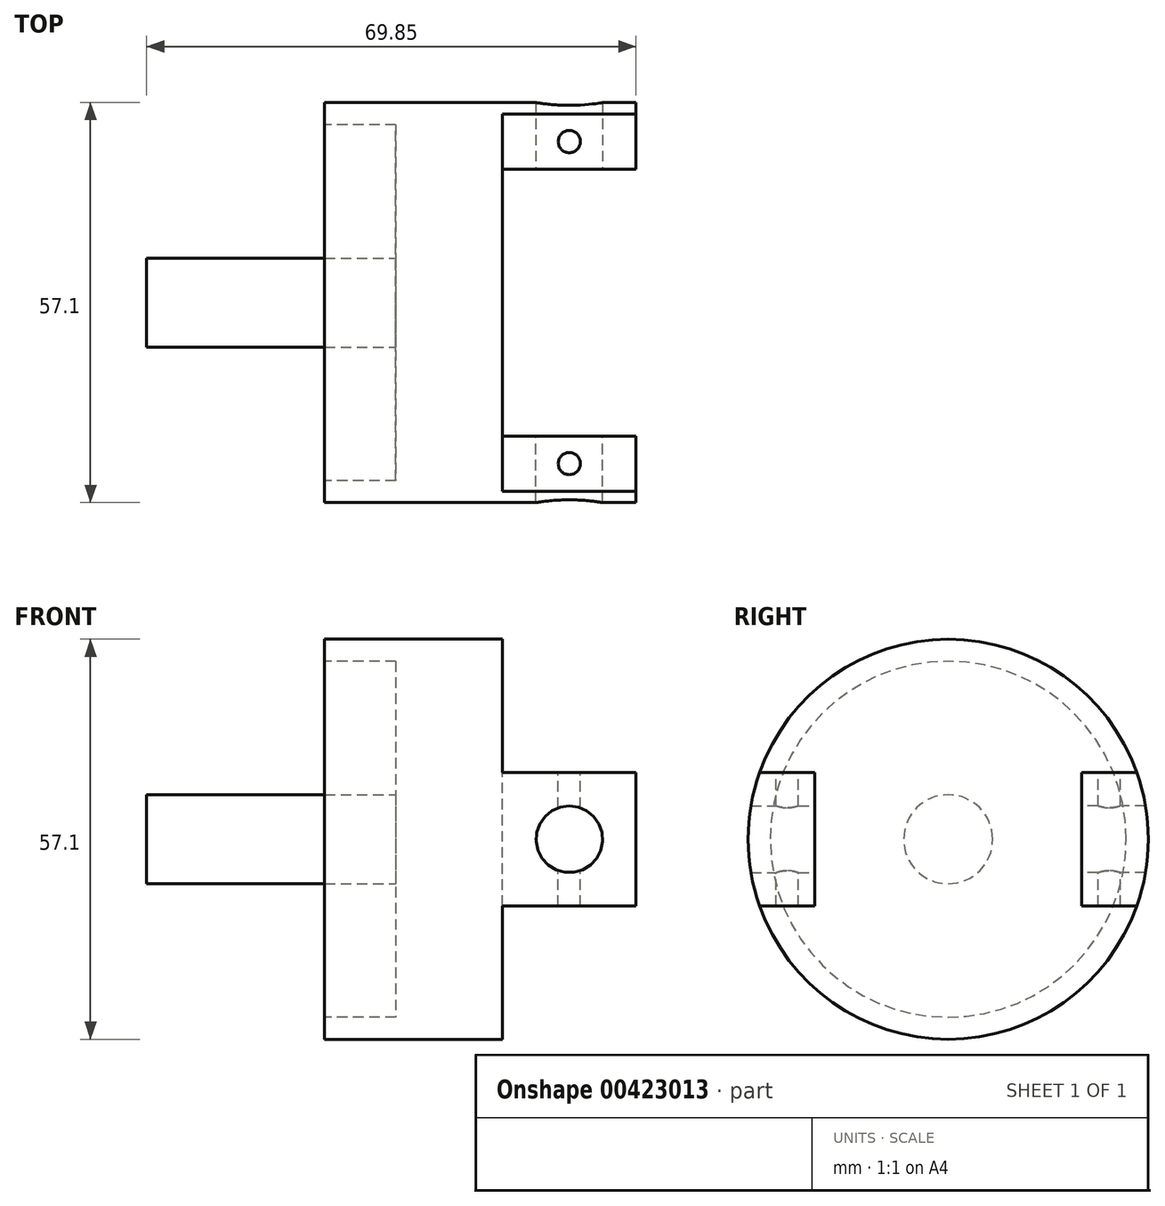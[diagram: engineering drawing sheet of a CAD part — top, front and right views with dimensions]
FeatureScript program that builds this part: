
annotation { "Feature Type Name" : "Feature", "Feature Type Description" : "" }
export const myFeature = defineFeature(function(context is Context, id is Id, definition is map)
    precondition{}
    {
        {
            var Q0;
            Q0=qCreatedBy(makeId("Right.planeOp"),FACE);
            var sketch = newSketch(context, id + "F0", { "sketchPlane" : qUnion([Q0])});
            skCircle(sketch, "E0", {"center": v(0, 0) * mm, "radius": 28.55 * mm});
            skSolve(sketch);
        }
        {
            var Q0;
            Q0 = qSketchRegion(id + "F0", true);
            extrude(context, id + "F1", {"entities" : qUnion([Q0]), "depth" : 38.1 * mm});
        }
        {
            var Q0;
            Q0=qCreatedBy(makeId("Front.planeOp"),FACE);
            var sketch = newSketch(context, id + "F2", { "sketchPlane" : qUnion([Q0])});
            skLineSegment(sketch, "E1.bottom", {"start": v(39.37, 31.7) * mm, "end": v(19.05, 31.7) * mm});
            skLineSegment(sketch, "E1.top", {"start": v(39.37, 9.53) * mm, "end": v(19.05, 9.53) * mm});
            skLineSegment(sketch, "E1.left", {"start": v(39.37, 31.7) * mm, "end": v(39.37, 9.53) * mm});
            skLineSegment(sketch, "E1.right", {"start": v(19.05, 31.7) * mm, "end": v(19.05, 9.53) * mm});
            skLineSegment(sketch, "E2.bottom", {"start": v(39.37, -9.53) * mm, "end": v(19.05, -9.53) * mm});
            skLineSegment(sketch, "E2.top", {"start": v(39.37, -31) * mm, "end": v(19.05, -31) * mm});
            skLineSegment(sketch, "E2.left", {"start": v(39.37, -9.53) * mm, "end": v(39.37, -31) * mm});
            skLineSegment(sketch, "E2.right", {"start": v(19.05, -9.53) * mm, "end": v(19.05, -31) * mm});
            skSolve(sketch);
        }
        {
            var Q0;
            Q0 = qSketchRegion(id + "F2", true);
            extrude(context, id + "F3", {"entities" : qUnion([Q0]), "operationType" : NewBodyOperationType.REMOVE, "oppositeDirection" : true, "depth" : 38.1 * mm, "hasSecondDirection" : true, "secondDirectionOppositeDirection" : false, "secondDirectionDepth" : 38.1 * mm});
        }
        {
            var Q0;
            Q0=qCreatedBy(makeId("Top.planeOp"),FACE);
            var sketch = newSketch(context, id + "F4", { "sketchPlane" : qUnion([Q0])});
            skLineSegment(sketch, "E3.bottom", {"start": v(64.66, 19.05) * mm, "end": v(19.05, 19.05) * mm});
            skLineSegment(sketch, "E3.top", {"start": v(64.66, -19.05) * mm, "end": v(19.05, -19.05) * mm});
            skLineSegment(sketch, "E3.left", {"start": v(64.66, 19.05) * mm, "end": v(64.66, -19.05) * mm});
            skLineSegment(sketch, "E3.right", {"start": v(19.05, 19.05) * mm, "end": v(19.05, -19.05) * mm});
            skPoint(sketch, "E3.middle", {"position": v(41.86, 0) * mm});
            skSolve(sketch);
        }
        {
            var Q0;
            Q0 = qSketchRegion(id + "F4", true);
            extrude(context, id + "F5", {"entities" : qUnion([Q0]), "operationType" : NewBodyOperationType.REMOVE, "oppositeDirection" : true, "depth" : 25.4 * mm, "hasSecondDirection" : true, "secondDirectionOppositeDirection" : false, "secondDirectionDepth" : 25.4 * mm});
        }
        {
            var Q0;
            Q0=makeQuery(id+"F5.boolean.opBoolean","COPY",FACE,{"derivedFrom":makeQuery(id+"F5.opExtrude","SWEPT_FACE",FACE,{"disambiguationData":[OSD([sQuery(id+"F4.wireOp",EDGE,"E3.bottom")])]})});
            var sketch = newSketch(context, id + "F6", { "sketchPlane" : qUnion([Q0])});
            skPoint(sketch, "E4", {"position": v(28.58, 0) * mm});
            skPoint(sketch, "E4.positionSnap0", {"position": v(28.58, 9.53) * mm});
            skSolve(sketch);
        }
        {
            var Q0;
            Q0=sQuery(id+"F6.wireOp",VERTEX,"E4");
            var Q1;
            Q1=makeQuery(id+"F1.opExtrude","SWEPT_BODY",BODY,{"disambiguationData":[OSD([sQuery(id+"F0.wireOp",EDGE,"E0")])]});
            hole(context, id + "F7", {"style" : HoleStyle.C_BORE, "endStyle" : HoleEndStyle.BLIND, "holeDiameter" : 9.52 * mm, "cBoreDiameter" : 9.52 * mm, "cBoreDepth" : 6.35 * mm, "holeDepth" : 25.4 * mm, "isTappedThrough" : true, "tappedDepth" : 12.7 * mm, "tapClearance" : 3, "locations" : qUnion([Q0]), "scope" : qUnion([Q1])});
        }
        {
            var Q0;
            Q0=makeQuery(id+"F5.boolean.opBoolean","COPY",FACE,{"derivedFrom":makeQuery(id+"F5.opExtrude","SWEPT_FACE",FACE,{"disambiguationData":[OSD([sQuery(id+"F4.wireOp",EDGE,"E3.top")])]})});
            var sketch = newSketch(context, id + "F8", { "sketchPlane" : qUnion([Q0])});
            skPoint(sketch, "E5", {"position": v(-28.57, 0) * mm});
            skPoint(sketch, "E5.positionSnap0", {"position": v(-28.57, 9.53) * mm});
            skSolve(sketch);
        }
        {
            var Q0;
            Q0=sQuery(id+"F8.wireOp",VERTEX,"E5");
            var Q1;
            Q1=makeQuery(id+"F1.opExtrude","SWEPT_BODY",BODY,{"disambiguationData":[OSD([sQuery(id+"F0.wireOp",EDGE,"E0")])]});
            hole(context, id + "F9", {"style" : HoleStyle.C_BORE, "endStyle" : HoleEndStyle.BLIND, "holeDiameter" : 9.52 * mm, "cBoreDiameter" : 9.52 * mm, "cBoreDepth" : 6.35 * mm, "holeDepth" : 25.4 * mm, "isTappedThrough" : true, "tappedDepth" : 12.7 * mm, "tapClearance" : 3, "locations" : qUnion([Q0]), "scope" : qUnion([Q1])});
        }
        {
            var Q0;
            Q0=makeQuery(id+"F5.boolean.opBoolean","SPLIT",FACE,{"disambiguationData":[TD([makeQuery(id+"F5.opExtrude","SWEPT_FACE",FACE,{"disambiguationData":[OSD([sQuery(id+"F4.wireOp",EDGE,"E3.bottom")])]})])],"derivedFrom":makeQuery(id+"F3.boolean.opBoolean","COPY",FACE,{"derivedFrom":makeQuery(id+"F3.opExtrude","SWEPT_FACE",FACE,{"disambiguationData":[OSD([sQuery(id+"F2.wireOp",EDGE,"E1.top")])]})})});
            var sketch = newSketch(context, id + "F10", { "sketchPlane" : qUnion([Q0])});
            skPoint(sketch, "E6", {"position": v(28.58, 22.98) * mm});
            skPoint(sketch, "E6.positionSnap0", {"position": v(38.1, 22.98) * mm});
            skPoint(sketch, "E6.positionSnap1", {"position": v(28.58, 26.91) * mm});
            skSolve(sketch);
        }
        {
            var Q0;
            Q0=makeQuery(id+"F5.boolean.opBoolean","SPLIT",FACE,{"disambiguationData":[TD([makeQuery(id+"F5.opExtrude","SWEPT_FACE",FACE,{"disambiguationData":[OSD([sQuery(id+"F4.wireOp",EDGE,"E3.top")])]})])],"derivedFrom":makeQuery(id+"F3.boolean.opBoolean","COPY",FACE,{"derivedFrom":makeQuery(id+"F3.opExtrude","SWEPT_FACE",FACE,{"disambiguationData":[OSD([sQuery(id+"F2.wireOp",EDGE,"E1.top")])]})})});
            var sketch = newSketch(context, id + "F11", { "sketchPlane" : qUnion([Q0])});
            skPoint(sketch, "E7", {"position": v(28.58, -22.98) * mm});
            skPoint(sketch, "E7.positionSnap0", {"position": v(38.1, -22.98) * mm});
            skPoint(sketch, "E7.positionSnap1", {"position": v(28.58, -19.05) * mm});
            skSolve(sketch);
        }
        {
            var Q0;
            Q0=sQuery(id+"F10.wireOp",VERTEX,"E6");
            var Q1;
            Q1=sQuery(id+"F11.wireOp",VERTEX,"E7");
            var Q2;
            Q2=makeQuery(id+"F1.opExtrude","SWEPT_BODY",BODY,{"disambiguationData":[OSD([sQuery(id+"F0.wireOp",EDGE,"E0")])]});
            hole(context, id + "F12", {"style" : HoleStyle.C_BORE, "endStyle" : HoleEndStyle.BLIND, "holeDiameter" : 3.17 * mm, "cBoreDiameter" : 3.17 * mm, "cBoreDepth" : 6.35 * mm, "holeDepth" : 25.4 * mm, "isTappedThrough" : true, "tappedDepth" : 12.7 * mm, "tapClearance" : 3, "locations" : qUnion([Q0, Q1]), "scope" : qUnion([Q2])});
        }
        {
            var Q0;
            Q0=makeQuery(id+"F1.opExtrude","CAP_FACE",FACE,{"disambiguationData":[OSD([sQuery(id+"F0.wireOp",EDGE,"E0")])],"isStart":true});
            var sketch = newSketch(context, id + "F13", { "sketchPlane" : qUnion([Q0])});
            skCircle(sketch, "E8", {"center": v(0, 0) * mm, "radius": 28.55 * mm});
            skSolve(sketch);
        }
        {
            var Q0;
            Q0 = qSketchRegion(id + "F13", true);
            extrude(context, id + "F14", {"entities" : qUnion([Q0]), "operationType" : NewBodyOperationType.ADD, "depth" : 6.35 * mm});
        }
        {
            var Q0;
            Q0=makeQuery(id+"F14.opExtrude","CAP_FACE",FACE,{"disambiguationData":[OSD([sQuery(id+"F13.wireOp",EDGE,"E8")])],"isStart":false});
            var sketch = newSketch(context, id + "F15", { "sketchPlane" : qUnion([Q0])});
            skCircle(sketch, "E9", {"center": v(0, 0) * mm, "radius": 6.35 * mm});
            skSolve(sketch);
        }
        {
            var Q0;
            Q0=makeQuery(id+"F15.imprint","IMPRINT",FACE,{"disambiguationData":[TD([[makeQuery(id+"F15.imprint","IMPRINT",EDGE,{"derivedFrom":sQuery(id+"F15.wireOp",EDGE,"E9")}),1.0]])]});
            extrude(context, id + "F16", {"entities" : qUnion([Q0]), "operationType" : NewBodyOperationType.ADD, "depth" : 25.4 * mm});
        }
        {
            var Q0;
            Q0=makeQuery(id+"F14.opExtrude","CAP_FACE",FACE,{"disambiguationData":[OSD([sQuery(id+"F13.wireOp",EDGE,"E8")])],"isStart":false});
            var sketch = newSketch(context, id + "F17", { "sketchPlane" : qUnion([Q0])});
            skCircle(sketch, "E10", {"center": v(0, 0) * mm, "radius": 25.4 * mm});
            skSolve(sketch);
        }
        {
            var Q0;
            Q0=makeQuery(id+"F17.imprint","IMPRINT",FACE,{"disambiguationData":[TD([[makeQuery(id+"F17.imprint","IMPRINT",EDGE,{"derivedFrom":sQuery(id+"F17.wireOp",EDGE,"E10")}),1.0]])]});
            extrude(context, id + "F18", {"entities" : qUnion([Q0]), "operationType" : NewBodyOperationType.REMOVE, "oppositeDirection" : true, "depth" : 10.16 * mm});
        }
    });
